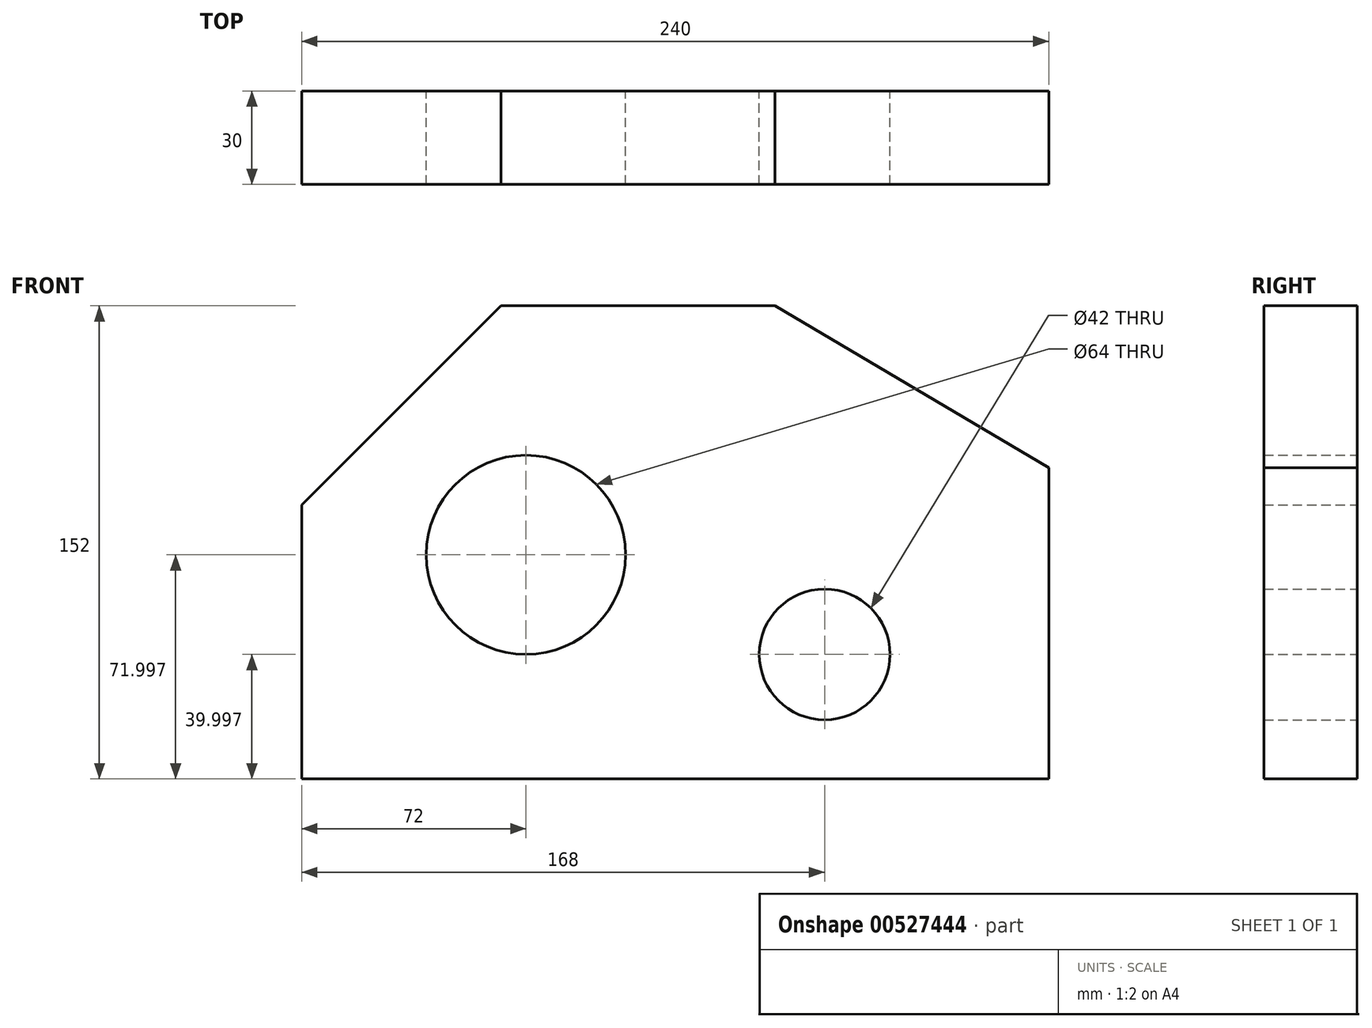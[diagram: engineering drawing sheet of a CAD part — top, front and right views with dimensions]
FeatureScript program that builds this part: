
annotation { "Feature Type Name" : "Feature", "Feature Type Description" : "" }
export const myFeature = defineFeature(function(context is Context, id is Id, definition is map)
    precondition{}
    {
        {
            var Q0;
            Q0=qCreatedBy(makeId("Front.planeOp"),FACE);
            var sketch = newSketch(context, id + "F0", { "sketchPlane" : qUnion([Q0])});
            skLineSegment(sketch, "E0", {"start": v(-116.25, 30.78) * mm, "end": v(-52.25, 94.78) * mm});
            skLineSegment(sketch, "E1", {"start": v(-52.25, 94.78) * mm, "end": v(35.75, 94.78) * mm});
            skLineSegment(sketch, "E2", {"start": v(35.75, 94.78) * mm, "end": v(123.75, 42.78) * mm});
            skLineSegment(sketch, "E3", {"start": v(123.75, 42.78) * mm, "end": v(123.75, -57.22) * mm});
            skLineSegment(sketch, "E4", {"start": v(123.75, -57.22) * mm, "end": v(-116.25, -57.22) * mm});
            skLineSegment(sketch, "E5", {"start": v(-116.25, -57.22) * mm, "end": v(-116.25, 30.78) * mm});
            skCircle(sketch, "E6", {"center": v(51.75, -17.22) * mm, "radius": 21 * mm});
            skCircle(sketch, "E7", {"center": v(-44.25, 14.78) * mm, "radius": 32 * mm});
            skSolve(sketch);
        }
        {
            var Q0;
            Q0=makeQuery(id+"F0.imprint","IMPRINT",FACE,{"disambiguationData":[TD([[makeQuery(id+"F0.imprint","IMPRINT",EDGE,{"derivedFrom":sQuery(id+"F0.wireOp",EDGE,"E0")}),-1.0]])]});
            extrude(context, id + "F1", {"entities" : qUnion([Q0]), "depth" : 30 * mm, "offsetDistance" : 25 * mm});
        }
    });
